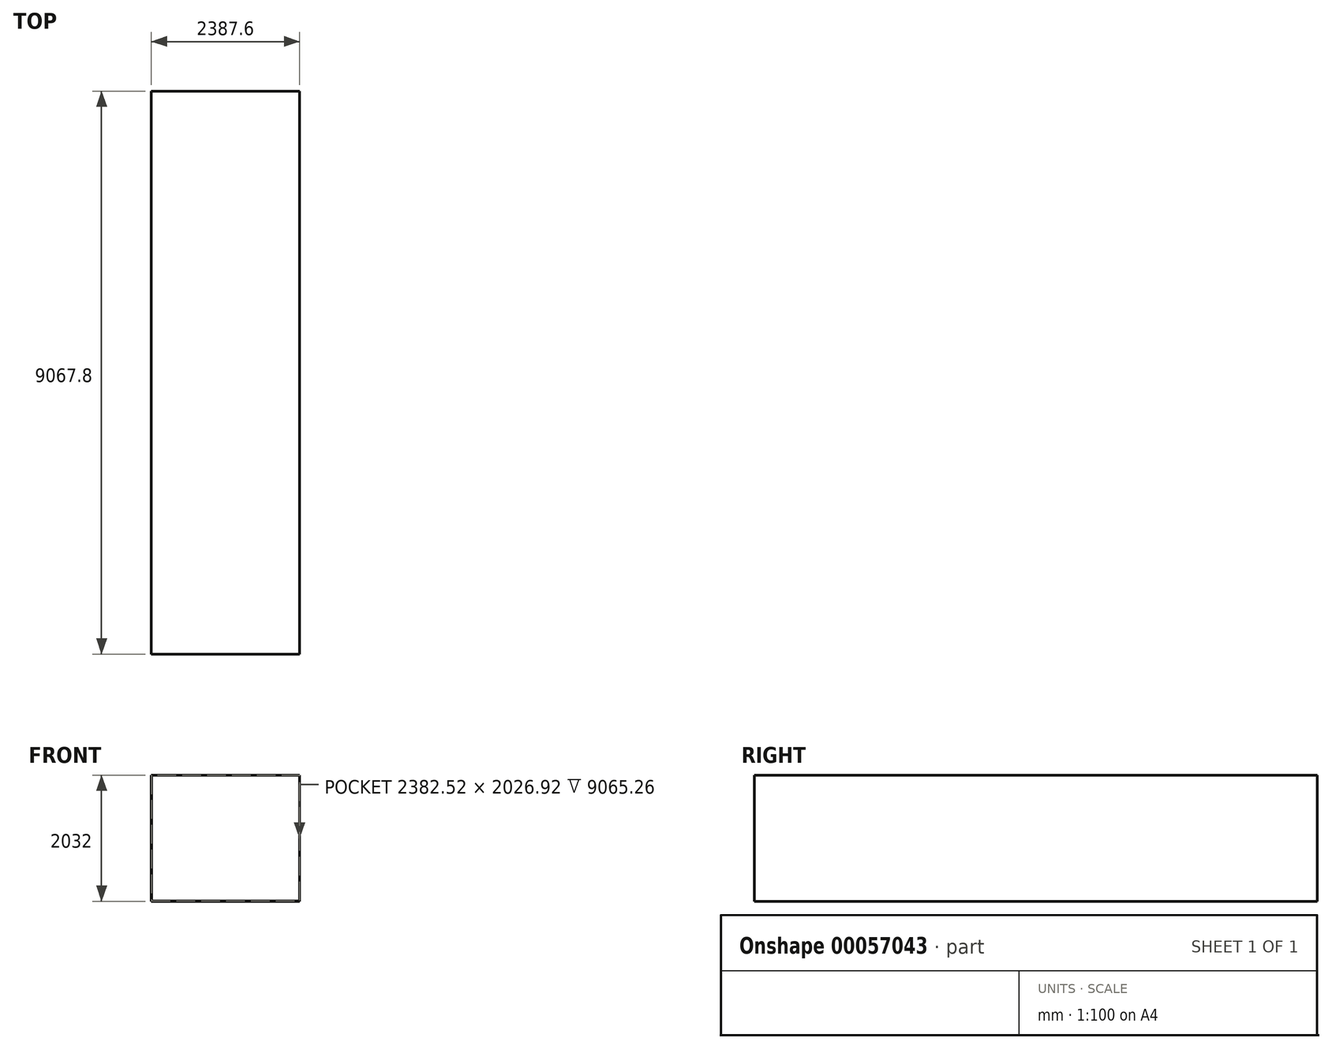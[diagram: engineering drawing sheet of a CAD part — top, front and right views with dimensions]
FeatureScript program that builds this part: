
annotation { "Feature Type Name" : "Feature", "Feature Type Description" : "" }
export const myFeature = defineFeature(function(context is Context, id is Id, definition is map)
    precondition{}
    {
        {
            var Q0;
            Q0=qCreatedBy(makeId("Front.planeOp"),FACE);
            var sketch = newSketch(context, id + "F0", { "sketchPlane" : qUnion([Q0])});
            skLineSegment(sketch, "E0.bottom", {"start": v(-137.14, 1921.85) * mm, "end": v(2250.46, 1921.85) * mm});
            skLineSegment(sketch, "E0.top", {"start": v(-137.14, -110.15) * mm, "end": v(2250.46, -110.15) * mm});
            skLineSegment(sketch, "E0.left", {"start": v(-137.14, 1921.85) * mm, "end": v(-137.14, -110.15) * mm});
            skLineSegment(sketch, "E0.right", {"start": v(2250.46, 1921.85) * mm, "end": v(2250.46, -110.15) * mm});
            skSolve(sketch);
        }
        {
            var Q0;
            Q0=makeQuery(id+"F0.imprint","IMPRINT",FACE,{"disambiguationData":[TD([[makeQuery(id+"F0.imprint","IMPRINT",EDGE,{"derivedFrom":sQuery(id+"F0.wireOp",EDGE,"E0.bottom")}),-1.0]])]});
            extrude(context, id + "F1", {"entities" : qUnion([Q0]), "depth" : 8839.2 * mm + 228.6 * mm});
        }
        {
            var Q0;
            Q0=makeQuery(id+"F1.opExtrude","CAP_FACE",FACE,{"disambiguationData":[OSD([sQuery(id+"F0.wireOp",EDGE,"E0.bottom"),sQuery(id+"F0.wireOp",EDGE,"E0.top"),sQuery(id+"F0.wireOp",EDGE,"E0.left"),sQuery(id+"F0.wireOp",EDGE,"E0.right")])],"isStart":false});
            shell(context, id + "F2", {"entities" : qUnion([Q0]), "thickness" : 2.54 * mm});
        }
    });
